# Revit family: Heatrae Sadia Multipoint Eco 80L & 100L V 3kW
name_source: partatom
category: Mechanical Equipment
revit_build: Autodesk Revit 2017 (Build: 20160225_1515(x64)
units: mm (PartAtom-declared; Revit-internal decimal feet)

## family parameters
Cut with Voids When Loaded = No
Host = Face
OmniClass Number = 23.65.35.11.11
OmniClass Title = Storage Water Heaters
Part Type = Normal
Room Calculation Point = No
Round Connector Dimension = Use Diameter
Shared = No

## types (2) — shared parameters
AboveClearanceZone = 300 mm
AssetType = Fixed
BelowClearanceZone = 300 mm
Category = Pr_60_60_96_28:Electric storage water heaters
ClearanceZoneMaterial = NBS_ClearanceZone
ColdWaterInletDiameter = 22 mm  [stored 0.0721785 ft]
Controls = Smart Thermostatic Control
Default Elevation = 1200 mm
DurationUnit = year
FlowRate = 20 l/min (minimum)
HasSwitch = Yes
HasTemperatureAndPressureReliefValve = Yes
HotWaterOutletDiameter = 22 mm  [stored 0.0721785 ft]
IfcExportAs = IfcBoilerType
IfcExportType = USERDEFINED
IsWaterStorageHeater = Yes
ManufacturerName = Heatrae Sadia Heating
ManufacturerURL = www.heatraesadia.com
Material = NBS_Concept
NBSCertification = www.nationalbimlibrary.com/cert/zja530o3
NBSDescription = Storage water heaters, electric
NominalEnergyConsumption = 6 mm  [stored 0.019685 ft]
OffsetFromWall = 12 mm  [stored 0.0393701 ft]
OutletTemperatureRange = 10°C to 70°C
PressureRating = 600 kPa
PressureReliefValvePosition1 = 179 mm
PressureReliefValvePosition2 = 186 mm  [stored 0.610236 ft]
ProductInformation = https://www.heatraesadia.com
Rating = 3 kW
Standards = EN55014-1:2017, EN55014-2:2015, EN60335-1:2012;A11:2014;A13:2017, EN60335-2-21:2003+A1:2005+A2:2008, EN61000-3-2:2014 & EN61000-3-3:2013, EN62233:2008, EN50440, EN60379
SupportPosition = 94 mm  [stored 0.308399 ft]
TemperatureAndPressureReliefValveConnectionDiameter = 15 mm  [stored 0.0492126 ft]
ThirdPartyCertification = NEMKO, Kiwa, CE
Uniclass2015Code = Pr_60_60_96_28
Uniclass2015Title = Electric storage water heaters
Uniclass2015Version = Products v1.7
Version = 2
WarrantyDurationParts = 2
WarrantyDurationUnit = year
WaterConnectionPosition = 83 mm  [stored 0.27231 ft]
zero-valued in all types: HeatOutput, NominalPartLoadRatio

## per-type parameters (varying)
| type | BIMObjectName | Capacity | CasingFinish | FrontClearanceZone | Height | LHSClearanceZone | Length | Name | NominalEfficiency | NominalHeight | NominalLength | NominalWidth | RHSClearanceZone | Size | WaterStorageCapacity | Weight | Width |
| Multipoint Eco 80L V 3kW | Heatrae Sadia Multipoint Eco 80V | 80 L |  | 300 mm | 966 mm  [stored 3.16929 ft] | 300 mm | 453 mm  [stored 1.48622 ft] | StorageWaterHeaters,Multipoint Eco 80L V 3kW | 39.9 | 1085 mm  [stored 3.55971 ft] | 465 mm  [stored 1.52559 ft] | 454 mm  [stored 1.4895 ft] | 300 mm | 453 x 454 x 966 mm | 80 L | 26 | 454 mm  [stored 1.4895 ft] |
| Multipoint Eco 100L V 3kW | Heatrae Sadia Multipoint Eco 100V | 100 L | White Enameled Steel | 0 mm  [stored 0 ft] | 1134 mm | 0 mm  [stored 0 ft] | 454 mm  [stored 1.4895 ft] | StorageWaterHeaters, Multipoint Eco 100L V 3kW | 38 | 1253 mm  [stored 4.11089 ft] | 466 mm  [stored 1.52887 ft] | 453 mm  [stored 1.48622 ft] | 0 mm  [stored 0 ft] | 453 x 454 x 1134 mm | 100 L | 30 | 453 mm  [stored 1.48622 ft] |

note: column(s) folded — value = type name in every type: ModelReference

note: [stored X ft] marks values corroborated as IEEE doubles in the binary element streams (Revit-internal decimal feet)

## geometry (parser evidence)
native form markers: Sweep x5
no freeform markers — native parametric forms only
